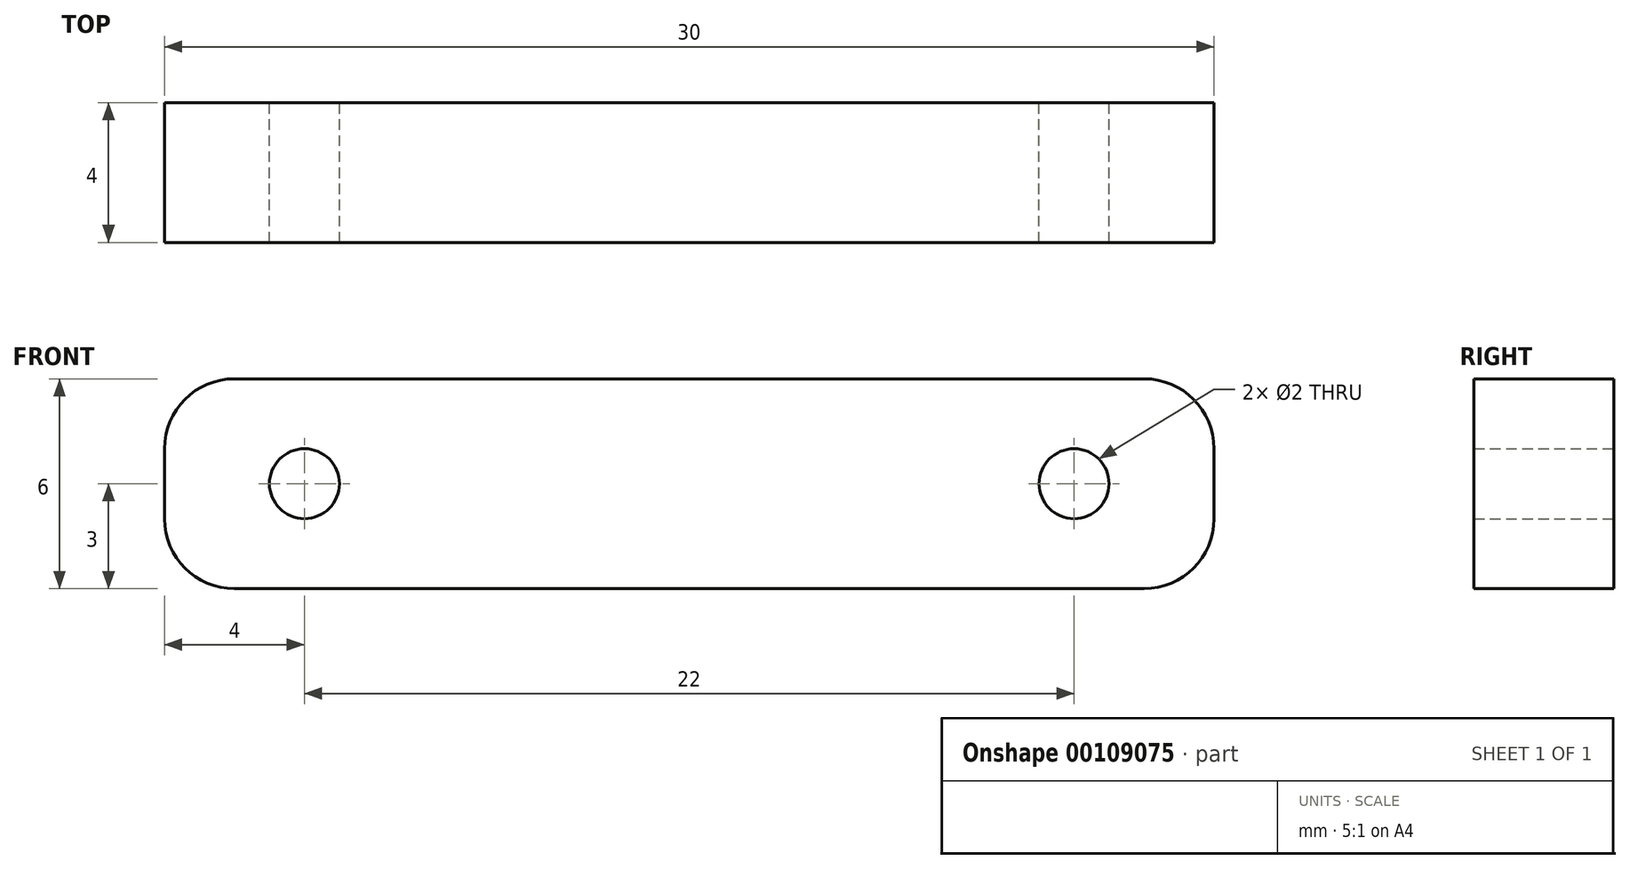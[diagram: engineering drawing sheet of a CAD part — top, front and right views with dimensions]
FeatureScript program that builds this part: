
annotation { "Feature Type Name" : "Feature", "Feature Type Description" : "" }
export const myFeature = defineFeature(function(context is Context, id is Id, definition is map)
    precondition{}
    {
        {
            var Q0;
            Q0=qCreatedBy(makeId("Front.planeOp"),FACE);
            var sketch = newSketch(context, id + "F0", { "sketchPlane" : qUnion([Q0])});
            skLineSegment(sketch, "E0.bottom", {"start": v(-13, 3) * mm, "end": v(13, 3) * mm});
            skLineSegment(sketch, "E0.top", {"start": v(-13, -3) * mm, "end": v(13, -3) * mm});
            skLineSegment(sketch, "E0.left", {"start": v(-15, 1) * mm, "end": v(-15, -1) * mm});
            skLineSegment(sketch, "E0.right", {"start": v(15, 1) * mm, "end": v(15, -1) * mm});
            skPoint(sketch, "E0.middle", {"position": v(0, 0) * mm});
            skPoint(sketch, "E1", {"position": v(-11, 0) * mm});
            skPoint(sketch, "E2", {"position": v(11, 0) * mm});
            skCircle(sketch, "E3", {"center": v(11, 0) * mm, "radius": 1 * mm});
            skCircle(sketch, "E4", {"center": v(-11, 0) * mm, "radius": 1 * mm});
            skPoint(sketch, "E5.visualSharp", {"position": v(-15, 3) * mm});
            skArc(sketch, "E5.filletArc", {"start": v(-13, 3) * mm, "mid": v(-14.41, 2.41) * mm, "end": v(-15, 1) * mm});
            skPoint(sketch, "E6.visualSharp", {"position": v(-15, -3) * mm});
            skArc(sketch, "E6.filletArc", {"start": v(-15, -1) * mm, "mid": v(-14.41, -2.41) * mm, "end": v(-13, -3) * mm});
            skPoint(sketch, "E7.visualSharp", {"position": v(15, 3) * mm});
            skArc(sketch, "E7.filletArc", {"start": v(15, 1) * mm, "mid": v(14.41, 2.41) * mm, "end": v(13, 3) * mm});
            skPoint(sketch, "E8.visualSharp", {"position": v(15, -3) * mm});
            skArc(sketch, "E8.filletArc", {"start": v(13, -3) * mm, "mid": v(14.41, -2.41) * mm, "end": v(15, -1) * mm});
            skSolve(sketch);
        }
        {
            var Q0;
            Q0 = qSketchRegion(id + "F0", true);
            extrude(context, id + "F1", {"entities" : qUnion([Q0]), "depth" : 4 * mm});
        }
    });
